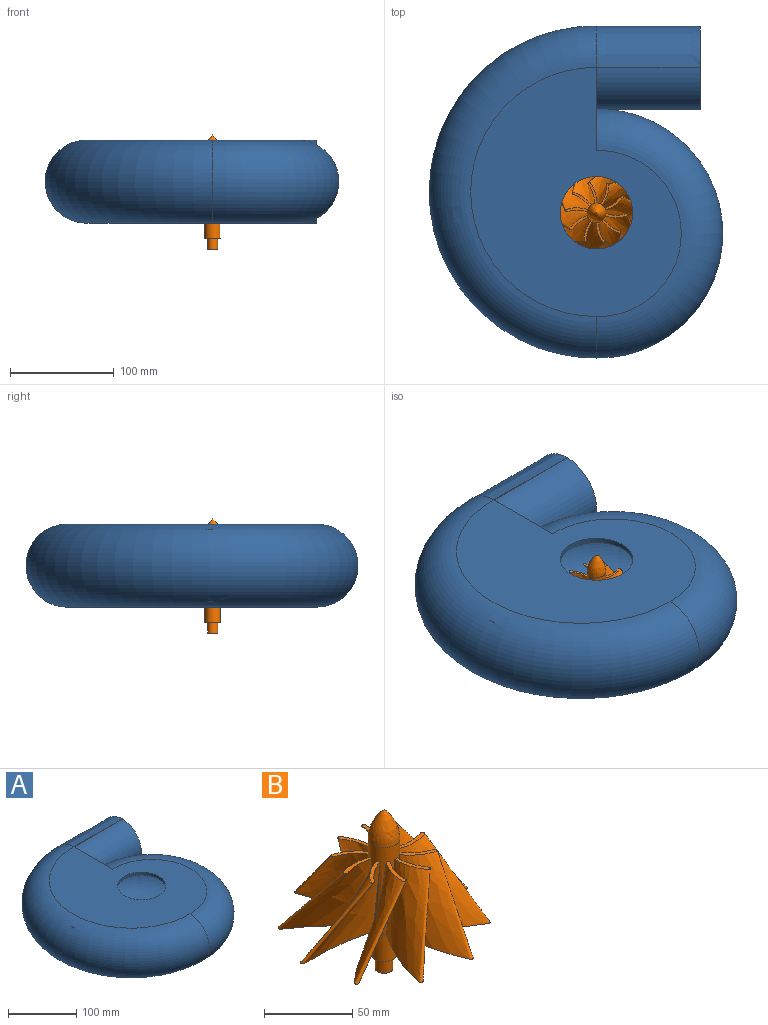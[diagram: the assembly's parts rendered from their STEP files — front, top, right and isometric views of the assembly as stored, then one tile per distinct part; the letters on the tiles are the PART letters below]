
ASSEMBLY  parts=2 mates=1
PART A: 36 faces, bbox 306.2x346.6x149.2 mm
  f0: plane 79.82x39.81mm, normal (1,0,0), area 686.4mm2, adj f4,f5,f14
  f1: torus R=140mm, axis (0,0,1), area 13128.3mm2, adj f3,f7,f11,f20,f24
  f2: plane 202.94x160.03mm, normal (0,0,1), area 22571.2mm2, adj f11,f12,f15,f19,f20,f21
  f3: plane 17.43x1.1mm, normal (0,0,1), area 0.5mm2, adj f1,f11
  f4: plane 240.02x221.26mm, normal (0,0,-1), area 33103.4mm2, adj f0,f5,f6,f9,f13,f14,f21
  f5: cylinder r=40mm len=100mm, axis (-1,0,0), area 6210.3mm2, adj f0,f4,f6,f10,f14
  f6: plane 80.01x80.01mm, normal (1,0,0), area 1178.3mm2, adj f4,f5,f7,f8,f9,f10,f25,f26
  f7: cylinder r=35mm len=100mm, axis (-1,0,0), area 10995.6mm2, adj f1,f6,f8,f27
  f8: extruded ~100x35mm, area 5497.9mm2, adj f6,f7,f11,f27
  f9: extruded ~100x40mm, area 6283.6mm2, adj f4,f6,f13,f28
  f10: extruded ~96.67x0.36mm, area 34.9mm2, adj f5,f6,f14,f29
  f11: torus R=120mm, axis (0,0,1), area 48266.7mm2, adj f1,f2,f3,f8,f12,f20,f23,f24
  f12: torus R=80.01mm, axis (0,0,1), area 35747.8mm2, adj f2,f11,f15,f23,f30
  f13: torus R=120mm, axis (0,0,1), area 57750.6mm2, adj f4,f9,f14,f16,f17,f18,f25,f28
  f14: torus R=80.01mm, axis (0,0,1), area 42054.6mm2, adj f0,f4,f5,f10,f13,f22,f25,f26
  f15: bspline ~95x95mm, area 6469.4mm2, adj f2,f12,f19,f20,f30
  f16: plane 5.69x0.82mm, normal (0,0,-1), area 2.3mm2, adj f13,f17,f18
  f17: torus R=140mm, axis (0,0,1), area 2.3mm2, adj f13,f16,f18
  f18: plane 0.82x0.01mm, normal (0,-1,0), area 0mm2, adj f13,f16,f17
  f19: plane 1.87x0.05mm, normal (0,-1,0), area 0mm2, adj f2,f15,f20
  f20: bspline ~149.04x82.03mm, area 4433.6mm2, adj f1,f2,f11,f15,f19,f23,f30,f34
  f21: cylinder r=7.5mm len=15mm, axis (0,0,1), area 235.6mm2, adj f2,f4
  f22: plane 79.82x39.81mm, normal (1,0,0), area 686.4mm2, adj f14,f25,f26
  f23: plane 202.94x160.03mm, normal (0,0,-1), area 18899.5mm2, adj f11,f12,f20,f30,f34,f35
  f24: plane 17.43x1.1mm, normal (0,0,-1), area 0.5mm2, adj f1,f11
  f25: plane 240.02x221.26mm, normal (0,0,1), area 29431.6mm2, adj f6,f13,f14,f22,f26,f28,f35
  f26: cylinder r=40mm len=100mm, axis (-1,0,0), area 6210.3mm2, adj f6,f14,f22,f25,f29
  f27: extruded ~100x35mm, area 5497.9mm2, adj f6,f7,f8,f11
  f28: extruded ~100x40mm, area 6283.6mm2, adj f6,f9,f13,f25
  f29: extruded ~96.67x0.36mm, area 34.9mm2, adj f6,f10,f14,f26
  f30: bspline ~95x95mm, area 6469.4mm2, adj f12,f15,f20,f23,f34
  f31: plane 5.69x0.82mm, normal (0,0,1), area 2.3mm2, adj f13,f32,f33
  f32: torus R=140mm, axis (0,0,-1), area 2.3mm2, adj f13,f31,f33
  f33: plane 0.82x0.01mm, normal (0,-1,0), area 0mm2, adj f13,f31,f32
  f34: plane 1.87x0.05mm, normal (0,-1,0), area 0mm2, adj f20,f23,f30
  f35: cylinder r=35mm len=70mm, axis (0,0,1), area 1099.6mm2, adj f23,f25
PART B: 27 faces, bbox 120.6x118.9x111.1 mm
  f0: plane 119.77x118.02mm, normal (0,0,-1), area 1733.3mm2, adj f3,f4,f7,f9,f11,f13,f15,f17
  f1: plane 10x10mm, normal (0,0,-1), area 78.5mm2, adj f6
  f2: revolved ~20x18mm, area 841.5mm2, adj f3
  f3: cylinder r=9mm len=60mm, axis (0,0,-1), area 2066.7mm2, adj f0,f2,f7,f8,f9,f10,f11,f12
  f4: cylinder r=7.5mm len=20mm, axis (0,0,-1), area 942.5mm2, adj f0,f5
  f5: plane 15x15mm, normal (0,0,-1), area 98.2mm2, adj f4,f6
  f6: cylinder r=5mm len=10mm, axis (0,0,-1), area 314.2mm2, adj f1,f5
  f7: bspline ~52.86x50mm, area 3844.8mm2, adj f0,f3,f8
  f8: plane 19.41x15.03mm, normal (0,0,1), area 48.8mm2, adj f3,f7
  f9: bspline ~50x47.63mm, area 3844.8mm2, adj f0,f3,f10
  f10: plane 21.69x9.55mm, normal (0,0,1), area 48.8mm2, adj f3,f9
  f11: bspline ~50x40.13mm, area 3844.8mm2, adj f0,f3,f12
  f12: plane 22.76x5.08mm, normal (0,0,1), area 48.8mm2, adj f3,f11
  f13: bspline ~52.86x50mm, area 3844.8mm2, adj f0,f3,f14
  f14: plane 19.41x15.03mm, normal (0,0,1), area 48.8mm2, adj f3,f13
  f15: bspline ~52.05x50mm, area 3834.1mm2, adj f0,f3,f16
  f16: plane 19.19x15.09mm, normal (0,0,1), area 48.8mm2, adj f3,f15
  f17: bspline ~50x40.13mm, area 3844.8mm2, adj f0,f3,f18
  f18: plane 22.76x5.08mm, normal (0,0,1), area 48.8mm2, adj f3,f17
  f19: bspline ~50x48.87mm, area 3844.8mm2, adj f0,f3,f20
  f20: plane 22.05x9.62mm, normal (0,0,1), area 48.8mm2, adj f3,f19
  f21: bspline ~50x47.63mm, area 3844.8mm2, adj f0,f3,f22
  f22: plane 21.69x9.55mm, normal (0,0,1), area 48.8mm2, adj f3,f21
  f23: bspline ~52.05x50mm, area 3844.8mm2, adj f0,f3,f24
  f24: plane 19.19x15.09mm, normal (0,0,1), area 48.8mm2, adj f3,f23
  f25: bspline ~50x48.87mm, area 3844.8mm2, adj f0,f3,f26
  f26: plane 22.05x9.62mm, normal (0,0,1), area 48.8mm2, adj f3,f25
PLACE A at identity fixed
PLACE B t=(0,0,-65)mm
MATE revolute B.f3 <-> A.f21  axis (0,0,-1) through (0,0,-35)mm
